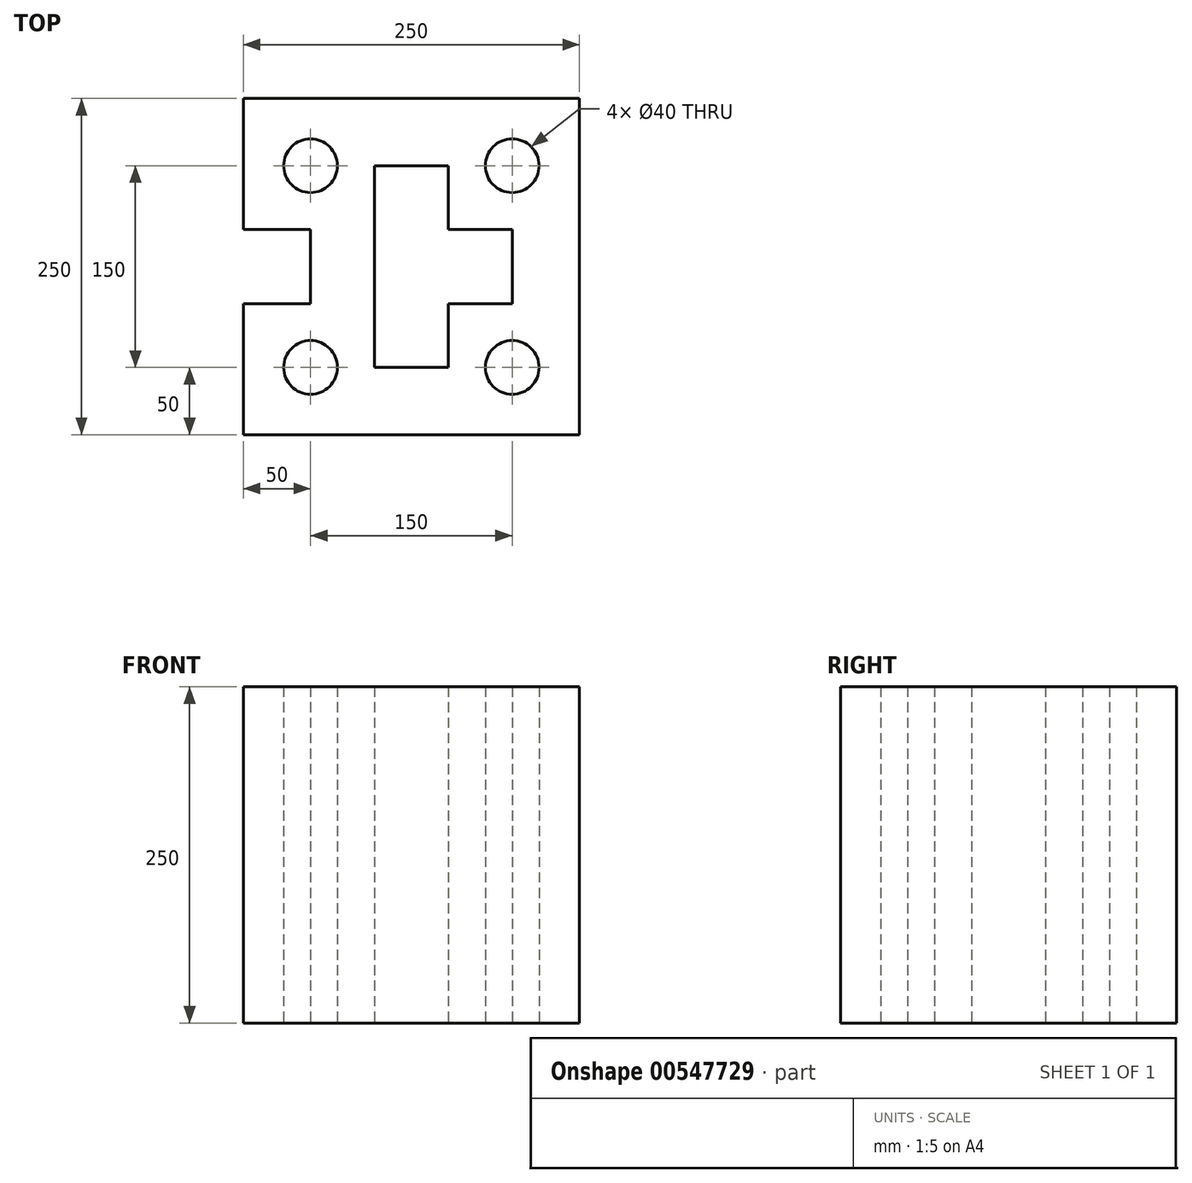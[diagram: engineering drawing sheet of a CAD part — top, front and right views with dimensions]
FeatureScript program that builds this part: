
annotation { "Feature Type Name" : "Feature", "Feature Type Description" : "" }
export const myFeature = defineFeature(function(context is Context, id is Id, definition is map)
    precondition{}
    {
        {
            var Q0;
            Q0=qCreatedBy(makeId("Top.planeOp"),FACE);
            var sketch = newSketch(context, id + "F0", { "sketchPlane" : qUnion([Q0])});
            skLineSegment(sketch, "E0", {"start": v(0, 0) * mm, "end": v(-200, 0) * mm, "construction": true});
            skLineSegment(sketch, "E1", {"start": v(0, 0) * mm, "end": v(0, 184.9) * mm, "construction": true});
            skLineSegment(sketch, "E2.bottom", {"start": v(125, 125) * mm, "end": v(-125, 125) * mm});
            skLineSegment(sketch, "E2.top", {"start": v(125, -125) * mm, "end": v(-125, -125) * mm});
            skLineSegment(sketch, "E2.left", {"start": v(125, 125) * mm, "end": v(125, -125) * mm});
            skLineSegment(sketch, "E2.right", {"start": v(-125, 125) * mm, "end": v(-125, 27.5) * mm});
            skLineSegment(sketch, "E3.bottom", {"start": v(-125, 27.5) * mm, "end": v(-75, 27.5) * mm});
            skLineSegment(sketch, "E3.top", {"start": v(-125, -27.5) * mm, "end": v(-75, -27.5) * mm});
            skLineSegment(sketch, "E3.right", {"start": v(-75, 27.5) * mm, "end": v(-75, -27.5) * mm});
            skPoint(sketch, "E3.middle", {"position": v(-100, 0) * mm});
            skLineSegment(sketch, "E4.trimOffspring", {"start": v(-125, -27.5) * mm, "end": v(-125, -125) * mm});
            skLineSegment(sketch, "E5", {"start": v(-27.5, 75) * mm, "end": v(-27.5, -75) * mm});
            skLineSegment(sketch, "E6", {"start": v(-27.5, -75) * mm, "end": v(27.5, -75) * mm});
            skLineSegment(sketch, "E7", {"start": v(27.5, -75) * mm, "end": v(27.5, -27.5) * mm});
            skLineSegment(sketch, "E8", {"start": v(27.5, -27.5) * mm, "end": v(75, -27.5) * mm});
            skLineSegment(sketch, "E9", {"start": v(75, -27.5) * mm, "end": v(75, 27.5) * mm});
            skLineSegment(sketch, "E10", {"start": v(75, 27.5) * mm, "end": v(27.5, 27.5) * mm});
            skLineSegment(sketch, "E11", {"start": v(27.5, 27.5) * mm, "end": v(27.5, 75) * mm});
            skLineSegment(sketch, "E12", {"start": v(27.5, 75) * mm, "end": v(-27.5, 75) * mm});
            skCircle(sketch, "E13", {"center": v(-75, 75) * mm, "radius": 20 * mm});
            skCircle(sketch, "E14", {"center": v(-75, -75) * mm, "radius": 20 * mm});
            skCircle(sketch, "E15", {"center": v(75, -75) * mm, "radius": 20 * mm});
            skCircle(sketch, "E16", {"center": v(75, 75) * mm, "radius": 20 * mm});
            skSolve(sketch);
        }
        {
            var Q0;
            Q0 = qSketchRegion(id + "F0", true);
            extrude(context, id + "F1", {"entities" : qUnion([Q0]), "endBound" : BoundingType.SYMMETRIC, "depth" : 250 * mm, "offsetDistance" : 25 * mm});
        }
    });
